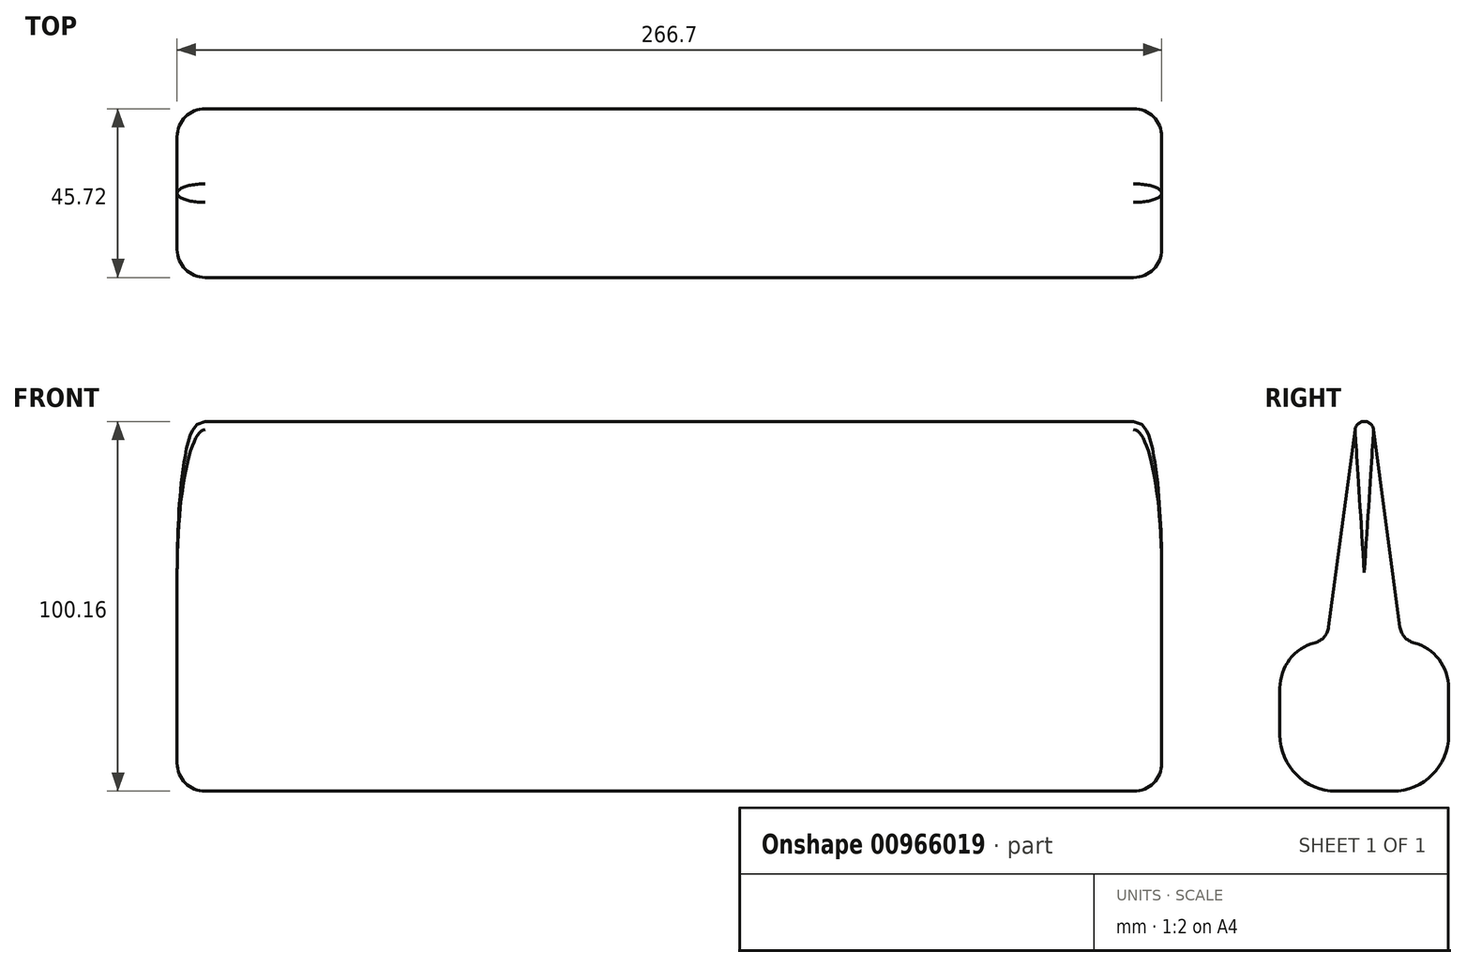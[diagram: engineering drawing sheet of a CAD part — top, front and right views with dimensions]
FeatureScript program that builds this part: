
annotation { "Feature Type Name" : "Feature", "Feature Type Description" : "" }
export const myFeature = defineFeature(function(context is Context, id is Id, definition is map)
    precondition{}
    {
        {
            var Q0;
            Q0=qCreatedBy(makeId("Top.planeOp"),FACE);
            var sketch = newSketch(context, id + "F0", { "sketchPlane" : qUnion([Q0])});
            skLineSegment(sketch, "E0.bottom", {"start": v(133.35, -22.86) * mm, "end": v(-133.35, -22.86) * mm});
            skLineSegment(sketch, "E0.top", {"start": v(133.35, 22.86) * mm, "end": v(-133.35, 22.86) * mm});
            skLineSegment(sketch, "E0.left", {"start": v(133.35, -22.86) * mm, "end": v(133.35, 22.86) * mm});
            skLineSegment(sketch, "E0.right", {"start": v(-133.35, -22.86) * mm, "end": v(-133.35, 22.86) * mm});
            skPoint(sketch, "E0.middle", {"position": v(0, 0) * mm});
            skSolve(sketch);
        }
        {
            var Q0;
            Q0=makeQuery(id+"F0.imprint","IMPRINT",FACE,{"disambiguationData":[TD([[makeQuery(id+"F0.imprint","IMPRINT",EDGE,{"derivedFrom":sQuery(id+"F0.wireOp",EDGE,"E0.bottom")}),-1.0]])]});
            var Q1;
            Q1 = qSketchRegion(id + "F0", true);
            extrude(context, id + "F1", {"entities" : qUnion([Q0, Q1]), "oppositeDirection" : true, "depth" : 40.64 * mm, "offsetDistance" : 25.4 * mm});
        }
        {
            var Q0;
            Q0=makeQuery(id+"F1.opExtrude","CAP_FACE",FACE,{"disambiguationData":[OSD([sQuery(id+"F0.wireOp",EDGE,"E0.bottom"),sQuery(id+"F0.wireOp",EDGE,"E0.top"),sQuery(id+"F0.wireOp",EDGE,"E0.left"),sQuery(id+"F0.wireOp",EDGE,"E0.right")])],"isStart":true});
            var sketch = newSketch(context, id + "F2", { "sketchPlane" : qUnion([Q0])});
            skLineSegment(sketch, "E1.bottom", {"start": v(-133.35, 10.16) * mm, "end": v(133.35, 10.16) * mm});
            skLineSegment(sketch, "E1.top", {"start": v(-133.35, -10.16) * mm, "end": v(133.35, -10.16) * mm});
            skLineSegment(sketch, "E1.left", {"start": v(-133.35, 10.16) * mm, "end": v(-133.35, -10.16) * mm});
            skLineSegment(sketch, "E1.right", {"start": v(133.35, 10.16) * mm, "end": v(133.35, -10.16) * mm});
            skSolve(sketch);
        }
        {
            var Q0;
            Q0=makeQuery(id+"F2.imprint","IMPRINT",FACE,{"disambiguationData":[TD([[makeQuery(id+"F2.imprint","IMPRINT",EDGE,{"derivedFrom":sQuery(id+"F2.wireOp",EDGE,"E1.bottom")}),-1.0]])]});
            extrude(context, id + "F3", {"entities" : qUnion([Q0]), "operationType" : NewBodyOperationType.ADD, "depth" : 76.2 * mm, "offsetDistance" : 25.4 * mm});
        }
        {
            var Q0;
            Q0=makeQuery(id+"F3.boolean.opBoolean","MERGE",FACE,{"derivedFrom":[makeQuery(id+"F1.opExtrude","SWEPT_FACE",FACE,{"disambiguationData":[OSD([sQuery(id+"F0.wireOp",EDGE,"E0.left")])]}),makeQuery(id+"F3.opExtrude","SWEPT_FACE",FACE,{"disambiguationData":[OSD([sQuery(id+"F2.wireOp",EDGE,"E1.right")])]})]});
            var sketch = newSketch(context, id + "F4", { "sketchPlane" : qUnion([Q0])});
            skLineSegment(sketch, "E2", {"start": v(10.16, 0) * mm, "end": v(0, 76.2) * mm});
            skLineSegment(sketch, "E3", {"start": v(0, 76.2) * mm, "end": v(-10.16, 0) * mm});
            skSolve(sketch);
        }
        {
            var Q0;
            {var subQ0=sQuery(id+"F4.wireOp",EDGE,"E3");Q0=makeQuery(id+"F4.imprint","IMPRINT",FACE,{"disambiguationData":[TD([[makeQuery(id+"F4.imprint","IMPRINT",EDGE,{"derivedFrom":subQ0}),-1.0]])]});}
            var Q1;
            {var subQ0=sQuery(id+"F4.wireOp",EDGE,"E2");Q1=makeQuery(id+"F4.imprint","IMPRINT",FACE,{"disambiguationData":[TD([[makeQuery(id+"F4.imprint","IMPRINT",EDGE,{"derivedFrom":subQ0}),-1.0]])]});}
            extrude(context, id + "F5", {"entities" : qUnion([Q0, Q1]), "operationType" : NewBodyOperationType.REMOVE, "oppositeDirection" : true, "depth" : 508 * mm, "offsetDistance" : 25.4 * mm});
        }
        {
            var Q0;
            {var subQ0=sQuery(id+"F4.wireOp",EDGE,"E3");var subQ1=sQuery(id+"F4.wireOp",EDGE,"E2");var subQ2=sQuery(id+"F2.wireOp",EDGE,"E1.right");Q0=makeQuery(id+"F5.boolean.opBoolean","MERGE",EDGE,{"derivedFrom":[],"fromTools":[makeQuery(id+"F5.opExtrude","SWEPT_EDGE",EDGE,{"disambiguationData":[OSD([subQ2,subQ1,subQ0]),OD(0.0)]}),makeQuery(id+"F5.opExtrude","SWEPT_EDGE",EDGE,{"disambiguationData":[OSD([subQ2,subQ1,subQ0]),OD(1.0)]})]});}
            fillet(context, id + "F6", {"entities" : qUnion([Q0]), "radius" : 2.54 * mm, "tangentPropagation" : true, "allowEdgeOverflow" : false});
        }
        {
            var Q0;
            Q0=makeQuery(id+"F1.opExtrude","CAP_EDGE",EDGE,{"disambiguationData":[OSD([sQuery(id+"F0.wireOp",EDGE,"E0.top")])],"isStart":true});
            var Q1;
            Q1=makeQuery(id+"F1.opExtrude","CAP_EDGE",EDGE,{"disambiguationData":[OSD([sQuery(id+"F0.wireOp",EDGE,"E0.bottom")])],"isStart":true});
            fillet(context, id + "F7", {"entities" : qUnion([Q0, Q1]), "radius" : 12.7 * mm, "tangentPropagation" : true, "allowEdgeOverflow" : false});
        }
        {
            var Q0;
            Q0=makeQuery(id+"F7.opFillet","BLEND_EDGE",EDGE,{"blendedFrom":[makeQuery(id+"F1.opExtrude","CAP_EDGE",EDGE,{"disambiguationData":[OSD([sQuery(id+"F0.wireOp",EDGE,"E0.top")])],"isStart":true}),makeQuery(id+"F5.boolean.opBoolean","COPY",FACE,{"derivedFrom":makeQuery(id+"F5.opExtrude","SWEPT_FACE",FACE,{"disambiguationData":[OSD([sQuery(id+"F4.wireOp",EDGE,"E2")])]})})],"blendedInto":[makeQuery(id+"F5.boolean.opBoolean","COPY",FACE,{"derivedFrom":makeQuery(id+"F5.opExtrude","SWEPT_FACE",FACE,{"disambiguationData":[OSD([sQuery(id+"F4.wireOp",EDGE,"E2")])]})})]});
            var Q1;
            Q1=makeQuery(id+"F7.opFillet","BLEND_EDGE",EDGE,{"blendedFrom":[makeQuery(id+"F1.opExtrude","CAP_EDGE",EDGE,{"disambiguationData":[OSD([sQuery(id+"F0.wireOp",EDGE,"E0.bottom")])],"isStart":true}),makeQuery(id+"F5.boolean.opBoolean","COPY",FACE,{"derivedFrom":makeQuery(id+"F5.opExtrude","SWEPT_FACE",FACE,{"disambiguationData":[OSD([sQuery(id+"F4.wireOp",EDGE,"E3")])]})})],"blendedInto":[makeQuery(id+"F5.boolean.opBoolean","COPY",FACE,{"derivedFrom":makeQuery(id+"F5.opExtrude","SWEPT_FACE",FACE,{"disambiguationData":[OSD([sQuery(id+"F4.wireOp",EDGE,"E3")])]})})]});
            fillet(context, id + "F8", {"entities" : qUnion([Q0, Q1]), "radius" : 5.08 * mm, "tangentPropagation" : true, "allowEdgeOverflow" : false});
        }
        {
            var Q0;
            Q0=makeQuery(id+"F1.opExtrude","CAP_EDGE",EDGE,{"disambiguationData":[OSD([sQuery(id+"F0.wireOp",EDGE,"E0.top")])],"isStart":false});
            var Q1;
            Q1=makeQuery(id+"F1.opExtrude","CAP_EDGE",EDGE,{"disambiguationData":[OSD([sQuery(id+"F0.wireOp",EDGE,"E0.bottom")])],"isStart":false});
            fillet(context, id + "F9", {"entities" : qUnion([Q0, Q1]), "radius" : 15.24 * mm, "tangentPropagation" : true, "allowEdgeOverflow" : false});
        }
        {
            var Q0;
            Q0=makeQuery(id+"F9.opFillet","BLEND_EDGE",EDGE,{"blendedFrom":[makeQuery(id+"F1.opExtrude","CAP_EDGE",EDGE,{"disambiguationData":[OSD([sQuery(id+"F0.wireOp",EDGE,"E0.top")])],"isStart":false}),makeQuery(id+"F3.boolean.opBoolean","MERGE",FACE,{"derivedFrom":[makeQuery(id+"F1.opExtrude","SWEPT_FACE",FACE,{"disambiguationData":[OSD([sQuery(id+"F0.wireOp",EDGE,"E0.left")])]}),makeQuery(id+"F3.opExtrude","SWEPT_FACE",FACE,{"disambiguationData":[OSD([sQuery(id+"F2.wireOp",EDGE,"E1.right")])]})]})],"blendedInto":[makeQuery(id+"F3.boolean.opBoolean","MERGE",FACE,{"derivedFrom":[makeQuery(id+"F1.opExtrude","SWEPT_FACE",FACE,{"disambiguationData":[OSD([sQuery(id+"F0.wireOp",EDGE,"E0.left")])]}),makeQuery(id+"F3.opExtrude","SWEPT_FACE",FACE,{"disambiguationData":[OSD([sQuery(id+"F2.wireOp",EDGE,"E1.right")])]})]})]});
            var Q1;
            Q1=makeQuery(id+"F5.boolean.opBoolean","INTERSECT",EDGE,{"derivedFrom":[makeQuery(id+"F3.boolean.opBoolean","MERGE",FACE,{"derivedFrom":[makeQuery(id+"F1.opExtrude","SWEPT_FACE",FACE,{"disambiguationData":[OSD([sQuery(id+"F0.wireOp",EDGE,"E0.right")])]}),makeQuery(id+"F3.opExtrude","SWEPT_FACE",FACE,{"disambiguationData":[OSD([sQuery(id+"F2.wireOp",EDGE,"E1.left")])]})]}),makeQuery(id+"F5.opExtrude","SWEPT_FACE",FACE,{"disambiguationData":[OSD([sQuery(id+"F4.wireOp",EDGE,"E2")])]})]});
            fillet(context, id + "F10", {"entities" : qUnion([Q0, Q1]), "radius" : 7.62 * mm, "tangentPropagation" : true, "allowEdgeOverflow" : false});
        }
    });
